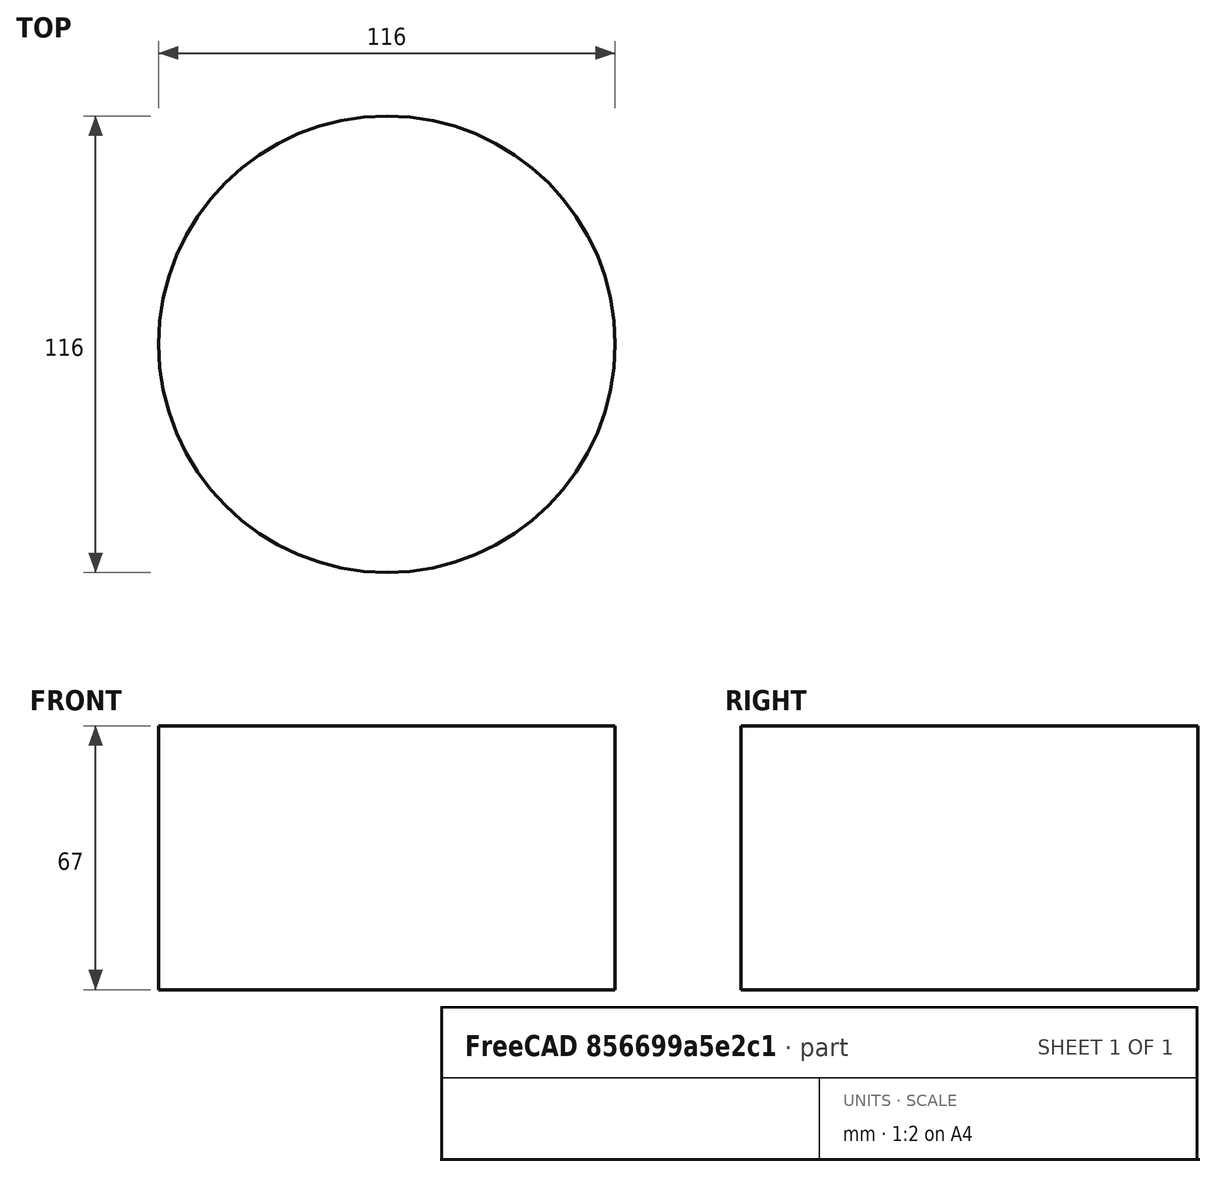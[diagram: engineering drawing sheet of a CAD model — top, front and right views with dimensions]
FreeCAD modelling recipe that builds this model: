
FCSTD DOCUMENT  (FreeCAD 1.1R38827 (Git))
Label: hub2108
License: All rights reserved
LicenseURL: http://en.wikipedia.org/wiki/All_rights_reserved
objects: Sketcher::SketchObject×5, PartDesign::CoordinateSystem×2, PartDesign::AdditiveCylinder×1, PartDesign::Body×1
note: 16 computed .brp shape members not serialized (recipe doc carries the construction recipe); baked Part::Feature solids carry a one-line shape summary decoded from their .brp

FEATURE [Sketcher::SketchObject] Sketch  label="top_fix_holes"
  ArcFitTolerance = 0
  FullyConstrained = true
  MakeInternals = false
  expr: Constraints[6] = (58.8 mm + 38 mm) / 2
  expr: Constraints[7] = (87.5 mm + 66.67 mm) / 2
  expr: Constraints[8] = (76.14 mm + 96.68 mm) / 2
  sketch-geometry (5):
    g0: Circle CenterX=38.5425 CenterY=-28.0433 CenterZ=0 NormalX=0 NormalY=0 NormalZ=1 AngleXU=0 Radius=5.1
    g1: Circle CenterX=43.205 CenterY=20.1316 CenterZ=0 NormalX=0 NormalY=0 NormalZ=1 AngleXU=0 Radius=5.1
    g2: Circle CenterX=-43.205 CenterY=20.1316 CenterZ=0 NormalX=0 NormalY=0 NormalZ=1 AngleXU=0 Radius=5.1
    g3: Circle CenterX=-38.5425 CenterY=-28.0433 CenterZ=0 NormalX=0 NormalY=0 NormalZ=1 AngleXU=0 Radius=5.1
    g4: Circle [constr] CenterX=0 CenterY=0 CenterZ=0 NormalX=0 NormalY=0 NormalZ=1 AngleXU=0 Radius=47.665
  constraints (13):
    c: Equal(g3,g2)
    c: Equal(g3,g1)
    c: Equal(g3,g0)
    c: Diameter(g3) = 10.2
    c: Symmetric(g0,g3,g-2)
    c: Symmetric(g1,g2,g-2)
    c: Distance(g0,g1) = 48.4
    c: Distance(g0,g3) = 77.085
    c: Distance(g2,g1) = 86.41
    c: Coincident(g4,g-1)
    c: PointOnObject(g0,g4)
    c: Distance(g3,g1) = 94.8866
    c: PointOnObject(g1,g4)
FEATURE [Sketcher::SketchObject] Sketch001  label="top_center_hole"
  ArcFitTolerance = 0
  FullyConstrained = true
  MakeInternals = false
  sketch-geometry (1):
    g0: Circle CenterX=0 CenterY=0 CenterZ=0 NormalX=0 NormalY=0 NormalZ=1 AngleXU=0 Radius=28
  constraints (2):
    c: Coincident(g0,g-1)
    c: Diameter(g0) = 56
FEATURE [Sketcher::SketchObject] Sketch002  label="bottom_fix_holes"
  ArcFitTolerance = 0
  FullyConstrained = true
  MakeInternals = false
  expr: Constraints[7] = (80 mm + 58.3 mm) / 4
  sketch-geometry (6):
    g0: Circle CenterX=34.575 CenterY=34.575 CenterZ=0 NormalX=0 NormalY=0 NormalZ=1 AngleXU=0 Radius=5.4
    g1: LineSegment [constr] StartX=34.575 StartY=34.575 StartZ=0 EndX=34.575 EndY=0 EndZ=0
    g2: LineSegment [constr] StartX=34.575 StartY=34.575 StartZ=0 EndX=0 EndY=34.575 EndZ=0
    g3: Circle CenterX=-34.575 CenterY=34.575 CenterZ=0 NormalX=0 NormalY=0 NormalZ=1 AngleXU=0 Radius=5.4
    g4: Circle CenterX=-34.575 CenterY=-34.575 CenterZ=0 NormalX=0 NormalY=0 NormalZ=1 AngleXU=0 Radius=5.4
    g5: Circle CenterX=34.575 CenterY=-34.575 CenterZ=0 NormalX=0 NormalY=0 NormalZ=1 AngleXU=0 Radius=5.4
  constraints (15):
    c: Coincident(g1,g0)
    c: PointOnObject(g1,g-1)
    c: Vertical(g1)
    c: Coincident(g2,g0)
    c: PointOnObject(g2,g-2)
    c: Horizontal(g2)
    c: Equal(g1,g2)
    c: DistanceY(g1,g1) = 34.575
    c: Diameter(g0) = 10.8
    c: Symmetric(g5,g0,g-1)
    c: Symmetric(g3,g0,g-2)
    c: Symmetric(g0,g4,g-1)
    c: Equal(g0,g5)
    c: Equal(g5,g4)
    c: Equal(g4,g3)
FEATURE [Sketcher::SketchObject] Sketch003  label="bottom_center_hole"
  ArcFitTolerance = 0
  FullyConstrained = true
  MakeInternals = false
  sketch-geometry (1):
    g0: Circle CenterX=0 CenterY=0 CenterZ=0 NormalX=0 NormalY=0 NormalZ=1 AngleXU=0 Radius=30.2
  constraints (2):
    c: Coincident(g0,g-1)
    c: Diameter(g0) = 60.4
FEATURE [PartDesign::AdditiveCylinder] Cylinder
  Angle = 360
  AttacherType = Attacher::AttachEngine3D
  AttachmentSupport = -> [XY_Plane]
  FirstAngle = 0
  Height = 67
  MapMode = 5
  Radius = 58
  SecondAngle = 0
  Suppressed = false
FEATURE [PartDesign::CoordinateSystem] Local_CS  label="bottom"
  AttacherType = Attacher::AttachEngine3D
  AttachmentSupport = -> [XY_Plane]
  MapMode = 5
FEATURE [PartDesign::CoordinateSystem] Local_CS001  label="top"
  AttacherType = Attacher::AttachEngine3D
  AttachmentOffset = pos=(0,0,67) rot=(0,0,1;0rad)
  AttachmentSupport = -> [XY_Plane]
  MapMode = 5
  Placement = pos=(0,0,67) rot=(0,0,1;0rad)
  expr: .AttachmentOffset.Base.z = Cylinder.Height
FEATURE [Sketcher::SketchObject] Sketch004
  ArcFitTolerance = 0
  AttachmentSupport = -> [XY_Plane]
  FullyConstrained = false
  MakeInternals = false
  MapMode = 5
  sketch-geometry (1):
    g0: Circle CenterX=0 CenterY=-2.41744 CenterZ=0 NormalX=0 NormalY=0 NormalZ=1 AngleXU=0 Radius=27.7935
  constraints (1):
    c: PointOnObject(g0,g-2)
FEATURE [PartDesign::Body] Body  label="hub2108"
  AllowCompound = false
  Group = -> [Cylinder,Local_CS,Local_CS001,Sketch004]
  Origin = -> Origin
  Tip = -> Cylinder
